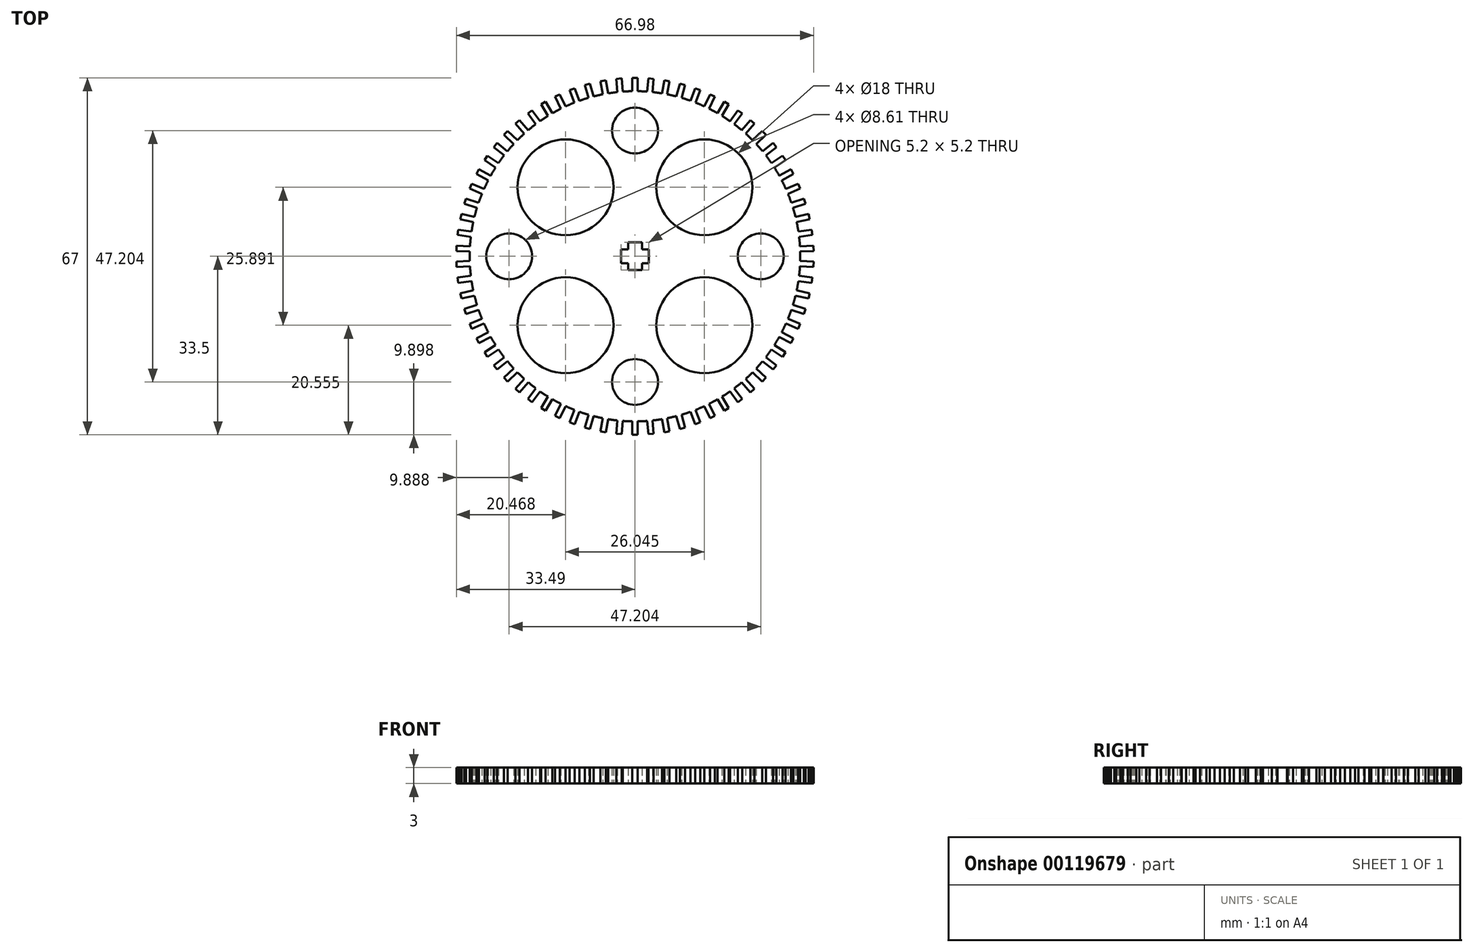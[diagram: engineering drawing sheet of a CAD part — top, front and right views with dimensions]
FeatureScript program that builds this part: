
annotation { "Feature Type Name" : "Feature", "Feature Type Description" : "" }
export const myFeature = defineFeature(function(context is Context, id is Id, definition is map)
    precondition{}
    {
        {
            var Q0;
            Q0=qCreatedBy(makeId("Top.planeOp"),FACE);
            var sketch = newSketch(context, id + "F0", { "sketchPlane" : qUnion([Q0])});
            skCircle(sketch, "E0", {"center": v(0, 0) * mm, "radius": 31 * mm});
            skLineSegment(sketch, "E1", {"start": v(0, 31) * mm, "end": v(0, 33.5) * mm});
            skLineSegment(sketch, "E2", {"start": v(0, 33.5) * mm, "end": v(0.5, 33.5) * mm});
            skLineSegment(sketch, "E3", {"start": v(0.5, 33.5) * mm, "end": v(0.5, 31) * mm});
            skLineSegment(sketch, "E4.MirrorCS", {"start": v(0, 33.5) * mm, "end": v(-0.5, 33.5) * mm});
            skLineSegment(sketch, "E5.MirrorCS", {"start": v(-0.5, 33.5) * mm, "end": v(-0.5, 31) * mm});
            skLineSegment(sketch, "E6.1.0", {"start": v(-2.5, 33.4) * mm, "end": v(-2.28, 30.92) * mm});
            skLineSegment(sketch, "E6.1.1", {"start": v(-3.5, 33.32) * mm, "end": v(-3.28, 30.83) * mm});
            skLineSegment(sketch, "E6.1.2", {"start": v(-3, 33.37) * mm, "end": v(-3.5, 33.32) * mm});
            skLineSegment(sketch, "E6.1.3", {"start": v(-3, 33.37) * mm, "end": v(-2.5, 33.4) * mm});
            skLineSegment(sketch, "E6.2.0", {"start": v(-5.49, 33.05) * mm, "end": v(-5.04, 30.59) * mm});
            skLineSegment(sketch, "E6.2.1", {"start": v(-6.47, 32.87) * mm, "end": v(-6.03, 30.4) * mm});
            skLineSegment(sketch, "E6.2.2", {"start": v(-5.98, 32.96) * mm, "end": v(-6.47, 32.87) * mm});
            skLineSegment(sketch, "E6.2.3", {"start": v(-5.98, 32.96) * mm, "end": v(-5.49, 33.05) * mm});
            skLineSegment(sketch, "E7.2.3.0", {"start": v(-8.43, 32.43) * mm, "end": v(-7.76, 30.01) * mm});
            skLineSegment(sketch, "E7.3.3.0", {"start": v(-9.4, 32.16) * mm, "end": v(-8.73, 29.75) * mm});
            skLineSegment(sketch, "E7.6.3.0", {"start": v(-8.91, 32.3) * mm, "end": v(-9.4, 32.16) * mm});
            skLineSegment(sketch, "E7.9.3.0", {"start": v(-8.91, 32.3) * mm, "end": v(-8.43, 32.43) * mm});
            skLineSegment(sketch, "E7.2.4.0", {"start": v(-11.3, 31.54) * mm, "end": v(-10.42, 29.2) * mm});
            skLineSegment(sketch, "E7.3.4.0", {"start": v(-12.24, 31.19) * mm, "end": v(-11.36, 28.84) * mm});
            skLineSegment(sketch, "E7.6.4.0", {"start": v(-11.77, 31.36) * mm, "end": v(-12.24, 31.19) * mm});
            skLineSegment(sketch, "E7.9.4.0", {"start": v(-11.77, 31.36) * mm, "end": v(-11.3, 31.54) * mm});
            skLineSegment(sketch, "E7.2.5.0", {"start": v(-14.08, 30.4) * mm, "end": v(-13, 28.14) * mm});
            skLineSegment(sketch, "E7.3.5.0", {"start": v(-14.99, 29.97) * mm, "end": v(-13.9, 27.7) * mm});
            skLineSegment(sketch, "E7.6.5.0", {"start": v(-14.54, 30.18) * mm, "end": v(-14.99, 29.97) * mm});
            skLineSegment(sketch, "E7.9.5.0", {"start": v(-14.54, 30.18) * mm, "end": v(-14.08, 30.4) * mm});
            skLineSegment(sketch, "E7.2.6.0", {"start": v(-16.75, 29.01) * mm, "end": v(-15.47, 26.86) * mm});
            skLineSegment(sketch, "E7.3.6.0", {"start": v(-17.61, 28.5) * mm, "end": v(-16.33, 26.35) * mm});
            skLineSegment(sketch, "E7.6.6.0", {"start": v(-17.18, 28.76) * mm, "end": v(-17.61, 28.5) * mm});
            skLineSegment(sketch, "E7.9.6.0", {"start": v(-17.18, 28.76) * mm, "end": v(-16.75, 29.01) * mm});
            skLineSegment(sketch, "E7.2.7.0", {"start": v(-19.29, 27.4) * mm, "end": v(-17.81, 25.37) * mm});
            skLineSegment(sketch, "E7.3.7.0", {"start": v(-20.1, 26.8) * mm, "end": v(-18.62, 24.78) * mm});
            skLineSegment(sketch, "E7.6.7.0", {"start": v(-19.7, 27.1) * mm, "end": v(-20.1, 26.8) * mm});
            skLineSegment(sketch, "E7.9.7.0", {"start": v(-19.7, 27.1) * mm, "end": v(-19.29, 27.4) * mm});
            skLineSegment(sketch, "E7.2.8.0", {"start": v(-21.66, 25.56) * mm, "end": v(-20.02, 23.67) * mm});
            skLineSegment(sketch, "E7.3.8.0", {"start": v(-22.42, 24.9) * mm, "end": v(-20.77, 23.01) * mm});
            skLineSegment(sketch, "E7.6.8.0", {"start": v(-22.04, 25.23) * mm, "end": v(-22.42, 24.9) * mm});
            skLineSegment(sketch, "E7.9.8.0", {"start": v(-22.04, 25.23) * mm, "end": v(-21.66, 25.56) * mm});
            skLineSegment(sketch, "E7.2.9.0", {"start": v(-23.87, 23.51) * mm, "end": v(-22.06, 21.78) * mm});
            skLineSegment(sketch, "E7.3.9.0", {"start": v(-24.56, 22.79) * mm, "end": v(-22.75, 21.06) * mm});
            skLineSegment(sketch, "E7.6.9.0", {"start": v(-24.21, 23.15) * mm, "end": v(-24.56, 22.79) * mm});
            skLineSegment(sketch, "E7.9.9.0", {"start": v(-24.21, 23.15) * mm, "end": v(-23.87, 23.51) * mm});
            skLineSegment(sketch, "E7.2.10.0", {"start": v(-25.88, 21.28) * mm, "end": v(-23.92, 19.72) * mm});
            skLineSegment(sketch, "E7.3.10.0", {"start": v(-26.5, 20.5) * mm, "end": v(-24.55, 18.93) * mm});
            skLineSegment(sketch, "E7.6.10.0", {"start": v(-26.2, 20.89) * mm, "end": v(-26.5, 20.5) * mm});
            skLineSegment(sketch, "E7.9.10.0", {"start": v(-26.2, 20.89) * mm, "end": v(-25.88, 21.28) * mm});
            skLineSegment(sketch, "E7.2.11.0", {"start": v(-27.68, 18.87) * mm, "end": v(-25.6, 17.5) * mm});
            skLineSegment(sketch, "E7.3.11.0", {"start": v(-28.23, 18.04) * mm, "end": v(-26.14, 16.66) * mm});
            skLineSegment(sketch, "E7.6.11.0", {"start": v(-27.96, 18.46) * mm, "end": v(-28.23, 18.04) * mm});
            skLineSegment(sketch, "E7.9.11.0", {"start": v(-27.96, 18.46) * mm, "end": v(-27.68, 18.87) * mm});
            skLineSegment(sketch, "E7.2.12.0", {"start": v(-29.26, 16.31) * mm, "end": v(-27.06, 15.13) * mm});
            skLineSegment(sketch, "E7.3.12.0", {"start": v(-29.74, 15.43) * mm, "end": v(-27.53, 14.25) * mm});
            skLineSegment(sketch, "E7.6.12.0", {"start": v(-29.5, 15.87) * mm, "end": v(-29.74, 15.43) * mm});
            skLineSegment(sketch, "E7.9.12.0", {"start": v(-29.5, 15.87) * mm, "end": v(-29.26, 16.31) * mm});
            skLineSegment(sketch, "E7.2.13.0", {"start": v(-30.6, 13.63) * mm, "end": v(-28.3, 12.64) * mm});
            skLineSegment(sketch, "E7.3.13.0", {"start": v(-31, 12.7) * mm, "end": v(-28.7, 11.72) * mm});
            skLineSegment(sketch, "E7.6.13.0", {"start": v(-30.8, 13.17) * mm, "end": v(-31, 12.7) * mm});
            skLineSegment(sketch, "E7.9.13.0", {"start": v(-30.8, 13.17) * mm, "end": v(-30.6, 13.63) * mm});
            skLineSegment(sketch, "E7.2.14.0", {"start": v(-31.7, 10.83) * mm, "end": v(-29.32, 10.05) * mm});
            skLineSegment(sketch, "E7.3.14.0", {"start": v(-32.01, 9.88) * mm, "end": v(-29.63, 9.1) * mm});
            skLineSegment(sketch, "E7.6.14.0", {"start": v(-31.86, 10.35) * mm, "end": v(-32.01, 9.88) * mm});
            skLineSegment(sketch, "E7.9.14.0", {"start": v(-31.86, 10.35) * mm, "end": v(-31.7, 10.83) * mm});
            skLineSegment(sketch, "E7.2.15.0", {"start": v(-32.55, 7.94) * mm, "end": v(-30.1, 7.38) * mm});
            skLineSegment(sketch, "E7.3.15.0", {"start": v(-32.77, 6.97) * mm, "end": v(-30.33, 6.4) * mm});
            skLineSegment(sketch, "E7.6.15.0", {"start": v(-32.66, 7.45) * mm, "end": v(-32.77, 6.97) * mm});
            skLineSegment(sketch, "E7.9.15.0", {"start": v(-32.66, 7.45) * mm, "end": v(-32.55, 7.94) * mm});
            skLineSegment(sketch, "E7.2.16.0", {"start": v(-33.13, 5) * mm, "end": v(-30.65, 4.66) * mm});
            skLineSegment(sketch, "E7.3.16.0", {"start": v(-33.26, 4) * mm, "end": v(-30.78, 3.67) * mm});
            skLineSegment(sketch, "E7.6.16.0", {"start": v(-33.2, 4.5) * mm, "end": v(-33.26, 4) * mm});
            skLineSegment(sketch, "E7.9.16.0", {"start": v(-33.2, 4.5) * mm, "end": v(-33.13, 5) * mm});
            skLineSegment(sketch, "E7.2.17.0", {"start": v(-33.44, 2) * mm, "end": v(-30.94, 1.9) * mm});
            skLineSegment(sketch, "E7.3.17.0", {"start": v(-33.49, 1) * mm, "end": v(-30.99, 0.9) * mm});
            skLineSegment(sketch, "E7.6.17.0", {"start": v(-33.47, 1.5) * mm, "end": v(-33.49, 1) * mm});
            skLineSegment(sketch, "E7.9.17.0", {"start": v(-33.47, 1.5) * mm, "end": v(-33.44, 2) * mm});
            skLineSegment(sketch, "E7.2.18.0", {"start": v(-33.49, -1) * mm, "end": v(-30.99, -0.9) * mm});
            skLineSegment(sketch, "E7.3.18.0", {"start": v(-33.44, -2) * mm, "end": v(-30.94, -1.9) * mm});
            skLineSegment(sketch, "E7.6.18.0", {"start": v(-33.47, -1.5) * mm, "end": v(-33.44, -2) * mm});
            skLineSegment(sketch, "E7.9.18.0", {"start": v(-33.47, -1.5) * mm, "end": v(-33.49, -1) * mm});
            skLineSegment(sketch, "E7.2.19.0", {"start": v(-33.26, -4) * mm, "end": v(-30.78, -3.67) * mm});
            skLineSegment(sketch, "E7.3.19.0", {"start": v(-33.13, -5) * mm, "end": v(-30.65, -4.66) * mm});
            skLineSegment(sketch, "E7.6.19.0", {"start": v(-33.2, -4.5) * mm, "end": v(-33.13, -5) * mm});
            skLineSegment(sketch, "E7.9.19.0", {"start": v(-33.2, -4.5) * mm, "end": v(-33.26, -4) * mm});
            skLineSegment(sketch, "E7.2.20.0", {"start": v(-32.77, -6.97) * mm, "end": v(-30.33, -6.4) * mm});
            skLineSegment(sketch, "E7.3.20.0", {"start": v(-32.55, -7.94) * mm, "end": v(-30.1, -7.38) * mm});
            skLineSegment(sketch, "E7.6.20.0", {"start": v(-32.66, -7.45) * mm, "end": v(-32.55, -7.94) * mm});
            skLineSegment(sketch, "E7.9.20.0", {"start": v(-32.66, -7.45) * mm, "end": v(-32.77, -6.97) * mm});
            skLineSegment(sketch, "E7.2.21.0", {"start": v(-32.01, -9.88) * mm, "end": v(-29.63, -9.1) * mm});
            skLineSegment(sketch, "E7.3.21.0", {"start": v(-31.7, -10.83) * mm, "end": v(-29.32, -10.05) * mm});
            skLineSegment(sketch, "E7.6.21.0", {"start": v(-31.86, -10.35) * mm, "end": v(-31.7, -10.83) * mm});
            skLineSegment(sketch, "E7.9.21.0", {"start": v(-31.86, -10.35) * mm, "end": v(-32.01, -9.88) * mm});
            skLineSegment(sketch, "E7.2.22.0", {"start": v(-31, -12.7) * mm, "end": v(-28.7, -11.72) * mm});
            skLineSegment(sketch, "E7.3.22.0", {"start": v(-30.6, -13.63) * mm, "end": v(-28.3, -12.64) * mm});
            skLineSegment(sketch, "E7.6.22.0", {"start": v(-30.8, -13.17) * mm, "end": v(-30.6, -13.63) * mm});
            skLineSegment(sketch, "E7.9.22.0", {"start": v(-30.8, -13.17) * mm, "end": v(-31, -12.7) * mm});
            skLineSegment(sketch, "E7.2.23.0", {"start": v(-29.74, -15.43) * mm, "end": v(-27.53, -14.25) * mm});
            skLineSegment(sketch, "E7.3.23.0", {"start": v(-29.26, -16.31) * mm, "end": v(-27.06, -15.13) * mm});
            skLineSegment(sketch, "E7.6.23.0", {"start": v(-29.5, -15.87) * mm, "end": v(-29.26, -16.31) * mm});
            skLineSegment(sketch, "E7.9.23.0", {"start": v(-29.5, -15.87) * mm, "end": v(-29.74, -15.43) * mm});
            skLineSegment(sketch, "E7.2.24.0", {"start": v(-28.23, -18.04) * mm, "end": v(-26.14, -16.66) * mm});
            skLineSegment(sketch, "E7.3.24.0", {"start": v(-27.68, -18.87) * mm, "end": v(-25.6, -17.5) * mm});
            skLineSegment(sketch, "E7.6.24.0", {"start": v(-27.96, -18.46) * mm, "end": v(-27.68, -18.87) * mm});
            skLineSegment(sketch, "E7.9.24.0", {"start": v(-27.96, -18.46) * mm, "end": v(-28.23, -18.04) * mm});
            skLineSegment(sketch, "E7.2.25.0", {"start": v(-26.5, -20.5) * mm, "end": v(-24.55, -18.93) * mm});
            skLineSegment(sketch, "E7.3.25.0", {"start": v(-25.88, -21.28) * mm, "end": v(-23.92, -19.72) * mm});
            skLineSegment(sketch, "E7.6.25.0", {"start": v(-26.2, -20.89) * mm, "end": v(-25.88, -21.28) * mm});
            skLineSegment(sketch, "E7.9.25.0", {"start": v(-26.2, -20.89) * mm, "end": v(-26.5, -20.5) * mm});
            skLineSegment(sketch, "E7.2.26.0", {"start": v(-24.56, -22.79) * mm, "end": v(-22.75, -21.06) * mm});
            skLineSegment(sketch, "E7.3.26.0", {"start": v(-23.87, -23.51) * mm, "end": v(-22.06, -21.78) * mm});
            skLineSegment(sketch, "E7.6.26.0", {"start": v(-24.21, -23.15) * mm, "end": v(-23.87, -23.51) * mm});
            skLineSegment(sketch, "E7.9.26.0", {"start": v(-24.21, -23.15) * mm, "end": v(-24.56, -22.79) * mm});
            skLineSegment(sketch, "E7.2.27.0", {"start": v(-22.42, -24.9) * mm, "end": v(-20.77, -23.01) * mm});
            skLineSegment(sketch, "E7.3.27.0", {"start": v(-21.66, -25.56) * mm, "end": v(-20.02, -23.67) * mm});
            skLineSegment(sketch, "E7.6.27.0", {"start": v(-22.04, -25.23) * mm, "end": v(-21.66, -25.56) * mm});
            skLineSegment(sketch, "E7.9.27.0", {"start": v(-22.04, -25.23) * mm, "end": v(-22.42, -24.9) * mm});
            skLineSegment(sketch, "E7.2.28.0", {"start": v(-20.1, -26.8) * mm, "end": v(-18.62, -24.78) * mm});
            skLineSegment(sketch, "E7.3.28.0", {"start": v(-19.29, -27.4) * mm, "end": v(-17.81, -25.37) * mm});
            skLineSegment(sketch, "E7.6.28.0", {"start": v(-19.7, -27.1) * mm, "end": v(-19.29, -27.4) * mm});
            skLineSegment(sketch, "E7.9.28.0", {"start": v(-19.7, -27.1) * mm, "end": v(-20.1, -26.8) * mm});
            skLineSegment(sketch, "E7.2.29.0", {"start": v(-17.61, -28.5) * mm, "end": v(-16.33, -26.35) * mm});
            skLineSegment(sketch, "E7.3.29.0", {"start": v(-16.75, -29.01) * mm, "end": v(-15.47, -26.86) * mm});
            skLineSegment(sketch, "E7.6.29.0", {"start": v(-17.18, -28.76) * mm, "end": v(-16.75, -29.01) * mm});
            skLineSegment(sketch, "E7.9.29.0", {"start": v(-17.18, -28.76) * mm, "end": v(-17.61, -28.5) * mm});
            skLineSegment(sketch, "E7.2.30.0", {"start": v(-14.99, -29.97) * mm, "end": v(-13.9, -27.7) * mm});
            skLineSegment(sketch, "E7.3.30.0", {"start": v(-14.08, -30.4) * mm, "end": v(-13, -28.14) * mm});
            skLineSegment(sketch, "E7.6.30.0", {"start": v(-14.54, -30.18) * mm, "end": v(-14.08, -30.4) * mm});
            skLineSegment(sketch, "E7.9.30.0", {"start": v(-14.54, -30.18) * mm, "end": v(-14.99, -29.97) * mm});
            skLineSegment(sketch, "E7.2.31.0", {"start": v(-12.24, -31.19) * mm, "end": v(-11.36, -28.84) * mm});
            skLineSegment(sketch, "E7.3.31.0", {"start": v(-11.3, -31.54) * mm, "end": v(-10.42, -29.2) * mm});
            skLineSegment(sketch, "E7.6.31.0", {"start": v(-11.77, -31.36) * mm, "end": v(-11.3, -31.54) * mm});
            skLineSegment(sketch, "E7.9.31.0", {"start": v(-11.77, -31.36) * mm, "end": v(-12.24, -31.19) * mm});
            skLineSegment(sketch, "E7.2.32.0", {"start": v(-9.4, -32.16) * mm, "end": v(-8.73, -29.75) * mm});
            skLineSegment(sketch, "E7.3.32.0", {"start": v(-8.43, -32.43) * mm, "end": v(-7.76, -30.01) * mm});
            skLineSegment(sketch, "E7.6.32.0", {"start": v(-8.91, -32.3) * mm, "end": v(-8.43, -32.43) * mm});
            skLineSegment(sketch, "E7.9.32.0", {"start": v(-8.91, -32.3) * mm, "end": v(-9.4, -32.16) * mm});
            skLineSegment(sketch, "E7.2.33.0", {"start": v(-6.47, -32.87) * mm, "end": v(-6.03, -30.4) * mm});
            skLineSegment(sketch, "E7.3.33.0", {"start": v(-5.49, -33.05) * mm, "end": v(-5.04, -30.59) * mm});
            skLineSegment(sketch, "E7.6.33.0", {"start": v(-5.98, -32.96) * mm, "end": v(-5.49, -33.05) * mm});
            skLineSegment(sketch, "E7.9.33.0", {"start": v(-5.98, -32.96) * mm, "end": v(-6.47, -32.87) * mm});
            skLineSegment(sketch, "E7.2.34.0", {"start": v(-3.5, -33.32) * mm, "end": v(-3.28, -30.83) * mm});
            skLineSegment(sketch, "E7.3.34.0", {"start": v(-2.5, -33.4) * mm, "end": v(-2.28, -30.92) * mm});
            skLineSegment(sketch, "E7.6.34.0", {"start": v(-3, -33.37) * mm, "end": v(-2.5, -33.4) * mm});
            skLineSegment(sketch, "E7.9.34.0", {"start": v(-3, -33.37) * mm, "end": v(-3.5, -33.32) * mm});
            skLineSegment(sketch, "E7.2.35.0", {"start": v(-0.5, -33.5) * mm, "end": v(-0.5, -31) * mm});
            skLineSegment(sketch, "E7.3.35.0", {"start": v(0.5, -33.5) * mm, "end": v(0.5, -31) * mm});
            skLineSegment(sketch, "E7.6.35.0", {"start": v(0, -33.5) * mm, "end": v(0.5, -33.5) * mm});
            skLineSegment(sketch, "E7.9.35.0", {"start": v(0, -33.5) * mm, "end": v(-0.5, -33.5) * mm});
            skLineSegment(sketch, "E7.2.36.0", {"start": v(2.5, -33.4) * mm, "end": v(2.28, -30.92) * mm});
            skLineSegment(sketch, "E7.3.36.0", {"start": v(3.5, -33.32) * mm, "end": v(3.28, -30.83) * mm});
            skLineSegment(sketch, "E7.6.36.0", {"start": v(3, -33.37) * mm, "end": v(3.5, -33.32) * mm});
            skLineSegment(sketch, "E7.9.36.0", {"start": v(3, -33.37) * mm, "end": v(2.5, -33.4) * mm});
            skLineSegment(sketch, "E7.2.37.0", {"start": v(5.49, -33.05) * mm, "end": v(5.04, -30.59) * mm});
            skLineSegment(sketch, "E7.3.37.0", {"start": v(6.47, -32.87) * mm, "end": v(6.03, -30.4) * mm});
            skLineSegment(sketch, "E7.6.37.0", {"start": v(5.98, -32.96) * mm, "end": v(6.47, -32.87) * mm});
            skLineSegment(sketch, "E7.9.37.0", {"start": v(5.98, -32.96) * mm, "end": v(5.49, -33.05) * mm});
            skLineSegment(sketch, "E7.2.38.0", {"start": v(8.43, -32.43) * mm, "end": v(7.76, -30.01) * mm});
            skLineSegment(sketch, "E7.3.38.0", {"start": v(9.4, -32.16) * mm, "end": v(8.73, -29.75) * mm});
            skLineSegment(sketch, "E7.6.38.0", {"start": v(8.91, -32.3) * mm, "end": v(9.4, -32.16) * mm});
            skLineSegment(sketch, "E7.9.38.0", {"start": v(8.91, -32.3) * mm, "end": v(8.43, -32.43) * mm});
            skLineSegment(sketch, "E7.2.39.0", {"start": v(11.3, -31.54) * mm, "end": v(10.42, -29.2) * mm});
            skLineSegment(sketch, "E7.3.39.0", {"start": v(12.24, -31.19) * mm, "end": v(11.36, -28.84) * mm});
            skLineSegment(sketch, "E7.6.39.0", {"start": v(11.77, -31.36) * mm, "end": v(12.24, -31.19) * mm});
            skLineSegment(sketch, "E7.9.39.0", {"start": v(11.77, -31.36) * mm, "end": v(11.3, -31.54) * mm});
            skLineSegment(sketch, "E7.2.40.0", {"start": v(14.08, -30.4) * mm, "end": v(13, -28.14) * mm});
            skLineSegment(sketch, "E7.3.40.0", {"start": v(14.99, -29.97) * mm, "end": v(13.9, -27.7) * mm});
            skLineSegment(sketch, "E7.6.40.0", {"start": v(14.54, -30.18) * mm, "end": v(14.99, -29.97) * mm});
            skLineSegment(sketch, "E7.9.40.0", {"start": v(14.54, -30.18) * mm, "end": v(14.08, -30.4) * mm});
            skLineSegment(sketch, "E7.2.41.0", {"start": v(16.75, -29.01) * mm, "end": v(15.47, -26.86) * mm});
            skLineSegment(sketch, "E7.3.41.0", {"start": v(17.61, -28.5) * mm, "end": v(16.33, -26.35) * mm});
            skLineSegment(sketch, "E7.6.41.0", {"start": v(17.18, -28.76) * mm, "end": v(17.61, -28.5) * mm});
            skLineSegment(sketch, "E7.9.41.0", {"start": v(17.18, -28.76) * mm, "end": v(16.75, -29.01) * mm});
            skLineSegment(sketch, "E7.2.42.0", {"start": v(19.29, -27.4) * mm, "end": v(17.81, -25.37) * mm});
            skLineSegment(sketch, "E7.3.42.0", {"start": v(20.1, -26.8) * mm, "end": v(18.62, -24.78) * mm});
            skLineSegment(sketch, "E7.6.42.0", {"start": v(19.7, -27.1) * mm, "end": v(20.1, -26.8) * mm});
            skLineSegment(sketch, "E7.9.42.0", {"start": v(19.7, -27.1) * mm, "end": v(19.29, -27.4) * mm});
            skLineSegment(sketch, "E7.2.43.0", {"start": v(21.66, -25.56) * mm, "end": v(20.02, -23.67) * mm});
            skLineSegment(sketch, "E7.3.43.0", {"start": v(22.42, -24.9) * mm, "end": v(20.77, -23.01) * mm});
            skLineSegment(sketch, "E7.6.43.0", {"start": v(22.04, -25.23) * mm, "end": v(22.42, -24.9) * mm});
            skLineSegment(sketch, "E7.9.43.0", {"start": v(22.04, -25.23) * mm, "end": v(21.66, -25.56) * mm});
            skLineSegment(sketch, "E7.2.44.0", {"start": v(23.87, -23.51) * mm, "end": v(22.06, -21.78) * mm});
            skLineSegment(sketch, "E7.3.44.0", {"start": v(24.56, -22.79) * mm, "end": v(22.75, -21.06) * mm});
            skLineSegment(sketch, "E7.6.44.0", {"start": v(24.21, -23.15) * mm, "end": v(24.56, -22.79) * mm});
            skLineSegment(sketch, "E7.9.44.0", {"start": v(24.21, -23.15) * mm, "end": v(23.87, -23.51) * mm});
            skLineSegment(sketch, "E7.2.45.0", {"start": v(25.88, -21.28) * mm, "end": v(23.92, -19.72) * mm});
            skLineSegment(sketch, "E7.3.45.0", {"start": v(26.5, -20.5) * mm, "end": v(24.55, -18.93) * mm});
            skLineSegment(sketch, "E7.6.45.0", {"start": v(26.2, -20.89) * mm, "end": v(26.5, -20.5) * mm});
            skLineSegment(sketch, "E7.9.45.0", {"start": v(26.2, -20.89) * mm, "end": v(25.88, -21.28) * mm});
            skLineSegment(sketch, "E7.2.46.0", {"start": v(27.68, -18.87) * mm, "end": v(25.6, -17.5) * mm});
            skLineSegment(sketch, "E7.3.46.0", {"start": v(28.23, -18.04) * mm, "end": v(26.14, -16.66) * mm});
            skLineSegment(sketch, "E7.6.46.0", {"start": v(27.96, -18.46) * mm, "end": v(28.23, -18.04) * mm});
            skLineSegment(sketch, "E7.9.46.0", {"start": v(27.96, -18.46) * mm, "end": v(27.68, -18.87) * mm});
            skLineSegment(sketch, "E7.2.47.0", {"start": v(29.26, -16.31) * mm, "end": v(27.06, -15.13) * mm});
            skLineSegment(sketch, "E7.3.47.0", {"start": v(29.74, -15.43) * mm, "end": v(27.53, -14.25) * mm});
            skLineSegment(sketch, "E7.6.47.0", {"start": v(29.5, -15.87) * mm, "end": v(29.74, -15.43) * mm});
            skLineSegment(sketch, "E7.9.47.0", {"start": v(29.5, -15.87) * mm, "end": v(29.26, -16.31) * mm});
            skLineSegment(sketch, "E7.2.48.0", {"start": v(30.6, -13.63) * mm, "end": v(28.3, -12.64) * mm});
            skLineSegment(sketch, "E7.3.48.0", {"start": v(31, -12.7) * mm, "end": v(28.7, -11.72) * mm});
            skLineSegment(sketch, "E7.6.48.0", {"start": v(30.8, -13.17) * mm, "end": v(31, -12.7) * mm});
            skLineSegment(sketch, "E7.9.48.0", {"start": v(30.8, -13.17) * mm, "end": v(30.6, -13.63) * mm});
            skLineSegment(sketch, "E7.2.49.0", {"start": v(31.7, -10.83) * mm, "end": v(29.32, -10.05) * mm});
            skLineSegment(sketch, "E7.3.49.0", {"start": v(32.01, -9.88) * mm, "end": v(29.63, -9.1) * mm});
            skLineSegment(sketch, "E7.6.49.0", {"start": v(31.86, -10.35) * mm, "end": v(32.01, -9.88) * mm});
            skLineSegment(sketch, "E7.9.49.0", {"start": v(31.86, -10.35) * mm, "end": v(31.7, -10.83) * mm});
            skLineSegment(sketch, "E7.2.50.0", {"start": v(32.55, -7.94) * mm, "end": v(30.1, -7.38) * mm});
            skLineSegment(sketch, "E7.3.50.0", {"start": v(32.77, -6.97) * mm, "end": v(30.33, -6.4) * mm});
            skLineSegment(sketch, "E7.6.50.0", {"start": v(32.66, -7.45) * mm, "end": v(32.77, -6.97) * mm});
            skLineSegment(sketch, "E7.9.50.0", {"start": v(32.66, -7.45) * mm, "end": v(32.55, -7.94) * mm});
            skLineSegment(sketch, "E7.2.51.0", {"start": v(33.13, -5) * mm, "end": v(30.65, -4.66) * mm});
            skLineSegment(sketch, "E7.3.51.0", {"start": v(33.26, -4) * mm, "end": v(30.78, -3.67) * mm});
            skLineSegment(sketch, "E7.6.51.0", {"start": v(33.2, -4.5) * mm, "end": v(33.26, -4) * mm});
            skLineSegment(sketch, "E7.9.51.0", {"start": v(33.2, -4.5) * mm, "end": v(33.13, -5) * mm});
            skLineSegment(sketch, "E7.2.52.0", {"start": v(33.44, -2) * mm, "end": v(30.94, -1.9) * mm});
            skLineSegment(sketch, "E7.3.52.0", {"start": v(33.49, -1) * mm, "end": v(30.99, -0.9) * mm});
            skLineSegment(sketch, "E7.6.52.0", {"start": v(33.47, -1.5) * mm, "end": v(33.49, -1) * mm});
            skLineSegment(sketch, "E7.9.52.0", {"start": v(33.47, -1.5) * mm, "end": v(33.44, -2) * mm});
            skLineSegment(sketch, "E7.2.53.0", {"start": v(33.49, 1) * mm, "end": v(30.99, 0.9) * mm});
            skLineSegment(sketch, "E7.3.53.0", {"start": v(33.44, 2) * mm, "end": v(30.94, 1.9) * mm});
            skLineSegment(sketch, "E7.6.53.0", {"start": v(33.47, 1.5) * mm, "end": v(33.44, 2) * mm});
            skLineSegment(sketch, "E7.9.53.0", {"start": v(33.47, 1.5) * mm, "end": v(33.49, 1) * mm});
            skLineSegment(sketch, "E7.2.54.0", {"start": v(33.26, 4) * mm, "end": v(30.78, 3.67) * mm});
            skLineSegment(sketch, "E7.3.54.0", {"start": v(33.13, 5) * mm, "end": v(30.65, 4.66) * mm});
            skLineSegment(sketch, "E7.6.54.0", {"start": v(33.2, 4.5) * mm, "end": v(33.13, 5) * mm});
            skLineSegment(sketch, "E7.9.54.0", {"start": v(33.2, 4.5) * mm, "end": v(33.26, 4) * mm});
            skLineSegment(sketch, "E7.2.55.0", {"start": v(32.77, 6.97) * mm, "end": v(30.33, 6.4) * mm});
            skLineSegment(sketch, "E7.3.55.0", {"start": v(32.55, 7.94) * mm, "end": v(30.1, 7.38) * mm});
            skLineSegment(sketch, "E7.6.55.0", {"start": v(32.66, 7.45) * mm, "end": v(32.55, 7.94) * mm});
            skLineSegment(sketch, "E7.9.55.0", {"start": v(32.66, 7.45) * mm, "end": v(32.77, 6.97) * mm});
            skLineSegment(sketch, "E7.2.56.0", {"start": v(32.01, 9.88) * mm, "end": v(29.63, 9.1) * mm});
            skLineSegment(sketch, "E7.3.56.0", {"start": v(31.7, 10.83) * mm, "end": v(29.32, 10.05) * mm});
            skLineSegment(sketch, "E7.6.56.0", {"start": v(31.86, 10.35) * mm, "end": v(31.7, 10.83) * mm});
            skLineSegment(sketch, "E7.9.56.0", {"start": v(31.86, 10.35) * mm, "end": v(32.01, 9.88) * mm});
            skLineSegment(sketch, "E7.2.57.0", {"start": v(31, 12.7) * mm, "end": v(28.7, 11.72) * mm});
            skLineSegment(sketch, "E7.3.57.0", {"start": v(30.6, 13.63) * mm, "end": v(28.3, 12.64) * mm});
            skLineSegment(sketch, "E7.6.57.0", {"start": v(30.8, 13.17) * mm, "end": v(30.6, 13.63) * mm});
            skLineSegment(sketch, "E7.9.57.0", {"start": v(30.8, 13.17) * mm, "end": v(31, 12.7) * mm});
            skLineSegment(sketch, "E7.2.58.0", {"start": v(29.74, 15.43) * mm, "end": v(27.53, 14.25) * mm});
            skLineSegment(sketch, "E7.3.58.0", {"start": v(29.26, 16.31) * mm, "end": v(27.06, 15.13) * mm});
            skLineSegment(sketch, "E7.6.58.0", {"start": v(29.5, 15.87) * mm, "end": v(29.26, 16.31) * mm});
            skLineSegment(sketch, "E7.9.58.0", {"start": v(29.5, 15.87) * mm, "end": v(29.74, 15.43) * mm});
            skLineSegment(sketch, "E7.2.59.0", {"start": v(28.23, 18.04) * mm, "end": v(26.14, 16.66) * mm});
            skLineSegment(sketch, "E7.3.59.0", {"start": v(27.68, 18.87) * mm, "end": v(25.6, 17.5) * mm});
            skLineSegment(sketch, "E7.6.59.0", {"start": v(27.96, 18.46) * mm, "end": v(27.68, 18.87) * mm});
            skLineSegment(sketch, "E7.9.59.0", {"start": v(27.96, 18.46) * mm, "end": v(28.23, 18.04) * mm});
            skLineSegment(sketch, "E7.2.60.0", {"start": v(26.5, 20.5) * mm, "end": v(24.55, 18.93) * mm});
            skLineSegment(sketch, "E7.3.60.0", {"start": v(25.88, 21.28) * mm, "end": v(23.92, 19.72) * mm});
            skLineSegment(sketch, "E7.6.60.0", {"start": v(26.2, 20.89) * mm, "end": v(25.88, 21.28) * mm});
            skLineSegment(sketch, "E7.9.60.0", {"start": v(26.2, 20.89) * mm, "end": v(26.5, 20.5) * mm});
            skLineSegment(sketch, "E7.2.61.0", {"start": v(24.56, 22.79) * mm, "end": v(22.75, 21.06) * mm});
            skLineSegment(sketch, "E7.3.61.0", {"start": v(23.87, 23.51) * mm, "end": v(22.06, 21.78) * mm});
            skLineSegment(sketch, "E7.6.61.0", {"start": v(24.21, 23.15) * mm, "end": v(23.87, 23.51) * mm});
            skLineSegment(sketch, "E7.9.61.0", {"start": v(24.21, 23.15) * mm, "end": v(24.56, 22.79) * mm});
            skLineSegment(sketch, "E7.2.62.0", {"start": v(22.42, 24.9) * mm, "end": v(20.77, 23.01) * mm});
            skLineSegment(sketch, "E7.3.62.0", {"start": v(21.66, 25.56) * mm, "end": v(20.02, 23.67) * mm});
            skLineSegment(sketch, "E7.6.62.0", {"start": v(22.04, 25.23) * mm, "end": v(21.66, 25.56) * mm});
            skLineSegment(sketch, "E7.9.62.0", {"start": v(22.04, 25.23) * mm, "end": v(22.42, 24.9) * mm});
            skLineSegment(sketch, "E7.2.63.0", {"start": v(20.1, 26.8) * mm, "end": v(18.62, 24.78) * mm});
            skLineSegment(sketch, "E7.3.63.0", {"start": v(19.29, 27.4) * mm, "end": v(17.81, 25.37) * mm});
            skLineSegment(sketch, "E7.6.63.0", {"start": v(19.7, 27.1) * mm, "end": v(19.29, 27.4) * mm});
            skLineSegment(sketch, "E7.9.63.0", {"start": v(19.7, 27.1) * mm, "end": v(20.1, 26.8) * mm});
            skLineSegment(sketch, "E7.2.64.0", {"start": v(17.61, 28.5) * mm, "end": v(16.33, 26.35) * mm});
            skLineSegment(sketch, "E7.3.64.0", {"start": v(16.75, 29.01) * mm, "end": v(15.47, 26.86) * mm});
            skLineSegment(sketch, "E7.6.64.0", {"start": v(17.18, 28.76) * mm, "end": v(16.75, 29.01) * mm});
            skLineSegment(sketch, "E7.9.64.0", {"start": v(17.18, 28.76) * mm, "end": v(17.61, 28.5) * mm});
            skLineSegment(sketch, "E7.2.65.0", {"start": v(14.99, 29.97) * mm, "end": v(13.9, 27.7) * mm});
            skLineSegment(sketch, "E7.3.65.0", {"start": v(14.08, 30.4) * mm, "end": v(13, 28.14) * mm});
            skLineSegment(sketch, "E7.6.65.0", {"start": v(14.54, 30.18) * mm, "end": v(14.08, 30.4) * mm});
            skLineSegment(sketch, "E7.9.65.0", {"start": v(14.54, 30.18) * mm, "end": v(14.99, 29.97) * mm});
            skLineSegment(sketch, "E7.2.66.0", {"start": v(12.24, 31.19) * mm, "end": v(11.36, 28.84) * mm});
            skLineSegment(sketch, "E7.3.66.0", {"start": v(11.3, 31.54) * mm, "end": v(10.42, 29.2) * mm});
            skLineSegment(sketch, "E7.6.66.0", {"start": v(11.77, 31.36) * mm, "end": v(11.3, 31.54) * mm});
            skLineSegment(sketch, "E7.9.66.0", {"start": v(11.77, 31.36) * mm, "end": v(12.24, 31.19) * mm});
            skLineSegment(sketch, "E7.2.67.0", {"start": v(9.4, 32.16) * mm, "end": v(8.73, 29.75) * mm});
            skLineSegment(sketch, "E7.3.67.0", {"start": v(8.43, 32.43) * mm, "end": v(7.76, 30.01) * mm});
            skLineSegment(sketch, "E7.6.67.0", {"start": v(8.91, 32.3) * mm, "end": v(8.43, 32.43) * mm});
            skLineSegment(sketch, "E7.9.67.0", {"start": v(8.91, 32.3) * mm, "end": v(9.4, 32.16) * mm});
            skLineSegment(sketch, "E7.2.68.0", {"start": v(6.47, 32.87) * mm, "end": v(6.03, 30.4) * mm});
            skLineSegment(sketch, "E7.3.68.0", {"start": v(5.49, 33.05) * mm, "end": v(5.04, 30.59) * mm});
            skLineSegment(sketch, "E7.6.68.0", {"start": v(5.98, 32.96) * mm, "end": v(5.49, 33.05) * mm});
            skLineSegment(sketch, "E7.9.68.0", {"start": v(5.98, 32.96) * mm, "end": v(6.47, 32.87) * mm});
            skLineSegment(sketch, "E7.2.69.0", {"start": v(3.5, 33.32) * mm, "end": v(3.28, 30.83) * mm});
            skLineSegment(sketch, "E7.3.69.0", {"start": v(2.5, 33.4) * mm, "end": v(2.28, 30.92) * mm});
            skLineSegment(sketch, "E7.6.69.0", {"start": v(3, 33.37) * mm, "end": v(2.5, 33.4) * mm});
            skLineSegment(sketch, "E7.9.69.0", {"start": v(3, 33.37) * mm, "end": v(3.5, 33.32) * mm});
            skCircle(sketch, "E8", {"center": v(-13.02, 12.95) * mm, "radius": 9 * mm});
            skLineSegment(sketch, "E9", {"start": v(0, 0) * mm, "end": v(0, 2.6) * mm, "construction": true});
            skLineSegment(sketch, "E10", {"start": v(0, 2.6) * mm, "end": v(-1.3, 2.6) * mm});
            skLineSegment(sketch, "E11", {"start": v(-1.3, 2.6) * mm, "end": v(-1.3, 1.3) * mm});
            skLineSegment(sketch, "E12", {"start": v(-1.3, 1.3) * mm, "end": v(-2.6, 1.3) * mm});
            skLineSegment(sketch, "E13", {"start": v(-2.6, 1.3) * mm, "end": v(-2.6, 0) * mm});
            skCircle(sketch, "E14.MirrorC", {"center": v(13.02, 12.95) * mm, "radius": 9 * mm});
            skLineSegment(sketch, "E15.MirrorCS", {"start": v(2.6, 1.3) * mm, "end": v(2.6, 0) * mm});
            skLineSegment(sketch, "E16.MirrorCS", {"start": v(1.3, 1.3) * mm, "end": v(2.6, 1.3) * mm});
            skLineSegment(sketch, "E17.MirrorCS", {"start": v(1.3, 2.6) * mm, "end": v(1.3, 1.3) * mm});
            skLineSegment(sketch, "E18.MirrorCS", {"start": v(0, 2.6) * mm, "end": v(1.3, 2.6) * mm});
            skLineSegment(sketch, "E19.MirrorCS", {"start": v(-2.6, -1.3) * mm, "end": v(-2.6, 0) * mm});
            skLineSegment(sketch, "E20.MirrorCS", {"start": v(-1.3, -1.3) * mm, "end": v(-2.6, -1.3) * mm});
            skLineSegment(sketch, "E21.MirrorCS", {"start": v(-1.3, -2.6) * mm, "end": v(-1.3, -1.3) * mm});
            skLineSegment(sketch, "E22.MirrorCS", {"start": v(0, -2.6) * mm, "end": v(-1.3, -2.6) * mm});
            skLineSegment(sketch, "E23.MirrorCS", {"start": v(2.6, -1.3) * mm, "end": v(2.6, 0) * mm});
            skLineSegment(sketch, "E24.MirrorCS", {"start": v(1.3, -1.3) * mm, "end": v(2.6, -1.3) * mm});
            skLineSegment(sketch, "E25.MirrorCS", {"start": v(1.3, -2.6) * mm, "end": v(1.3, -1.3) * mm});
            skLineSegment(sketch, "E26.MirrorCS", {"start": v(0, -2.6) * mm, "end": v(1.3, -2.6) * mm});
            skCircle(sketch, "E27.MirrorC", {"center": v(-13.02, -12.95) * mm, "radius": 9 * mm});
            skCircle(sketch, "E28.MirrorC", {"center": v(13.02, -12.95) * mm, "radius": 9 * mm});
            skCircle(sketch, "E29", {"center": v(-23.6, 0) * mm, "radius": 4.3 * mm});
            skCircle(sketch, "E30.1.0", {"center": v(0, -23.6) * mm, "radius": 4.3 * mm});
            skCircle(sketch, "E30.2.0", {"center": v(23.6, 0) * mm, "radius": 4.3 * mm});
            skCircle(sketch, "E31.1.3.0", {"center": v(0, 23.6) * mm, "radius": 4.3 * mm});
            skLineSegment(sketch, "E32", {"start": v(0, 33.5) * mm, "end": v(0, -33.5) * mm, "construction": true});
            skSolve(sketch);
        }
        {
            var Q0;
            Q0 = qSketchRegion(id + "F0", true);
            extrude(context, id + "F1", {"entities" : qUnion([Q0]), "depth" : 3 * mm});
        }
    });
